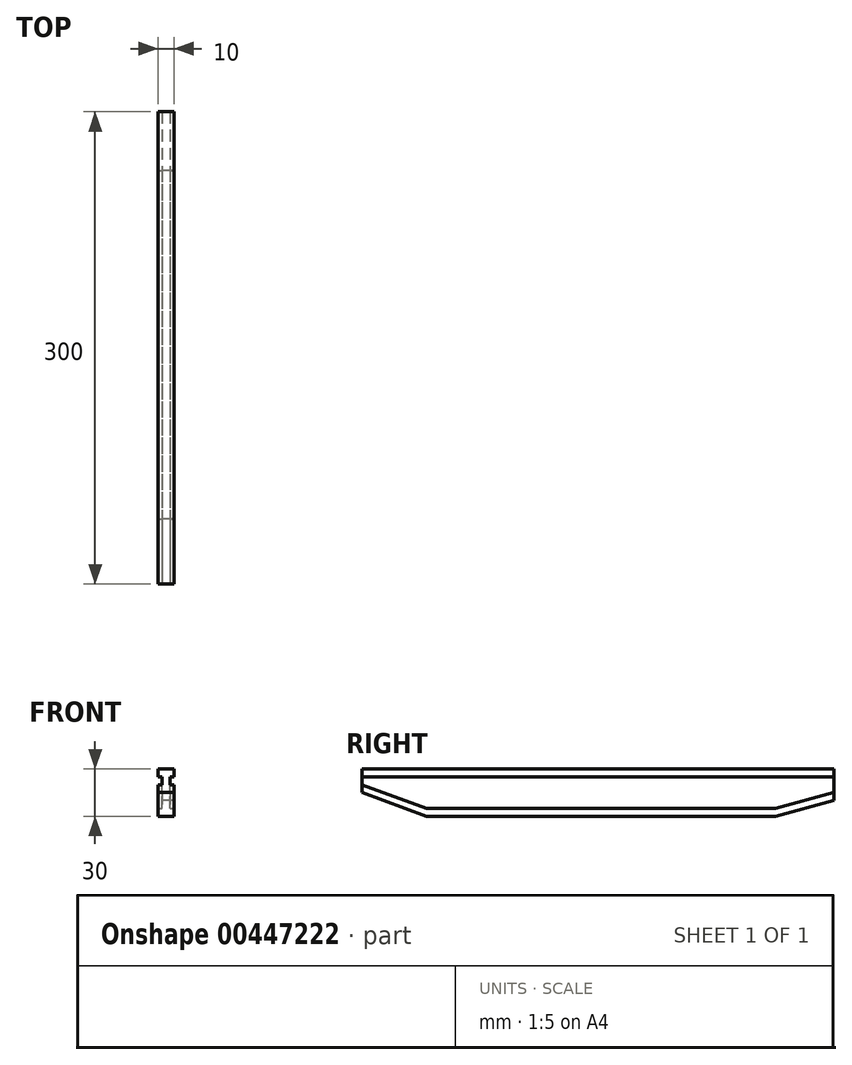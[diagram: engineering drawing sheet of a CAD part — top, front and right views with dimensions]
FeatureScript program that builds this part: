
annotation { "Feature Type Name" : "Feature", "Feature Type Description" : "" }
export const myFeature = defineFeature(function(context is Context, id is Id, definition is map)
    precondition{}
    {
        {
            var Q0;
            Q0=qCreatedBy(makeId("Right.planeOp"),FACE);
            var sketch = newSketch(context, id + "F0", { "sketchPlane" : qUnion([Q0])});
            skLineSegment(sketch, "E0", {"start": v(0, 0) * mm, "end": v(-300, 0) * mm});
            skLineSegment(sketch, "E1", {"start": v(-300, 0) * mm, "end": v(-300, -15) * mm});
            skLineSegment(sketch, "E2", {"start": v(-300, -15) * mm, "end": v(-258.79, -30) * mm});
            skLineSegment(sketch, "E3", {"start": v(-258.79, -30) * mm, "end": v(-37.32, -30) * mm});
            skLineSegment(sketch, "E4", {"start": v(-37.32, -30) * mm, "end": v(0, -20) * mm});
            skLineSegment(sketch, "E5", {"start": v(0, -20) * mm, "end": v(0, 0) * mm});
            skSolve(sketch);
        }
        {
            var Q0;
            Q0 = qSketchRegion(id + "F0", true);
            extrude(context, id + "F1", {"entities" : qUnion([Q0]), "endBound" : BoundingType.SYMMETRIC, "depth" : 5 * mm, "offsetDistance" : 25 * mm});
        }
        {
            var Q0;
            Q0=qCreatedBy(makeId("Front.planeOp"),FACE);
            var sketch = newSketch(context, id + "F2", { "sketchPlane" : qUnion([Q0])});
            skLineSegment(sketch, "E6.bottom", {"start": v(-5, 0) * mm, "end": v(5, 0) * mm});
            skLineSegment(sketch, "E6.top", {"start": v(-5, -5) * mm, "end": v(5, -5) * mm});
            skLineSegment(sketch, "E6.left", {"start": v(-5, 0) * mm, "end": v(-5, -5) * mm});
            skLineSegment(sketch, "E6.right", {"start": v(5, 0) * mm, "end": v(5, -5) * mm});
            skPoint(sketch, "E6.middle", {"position": v(0, -2.5) * mm});
            skSolve(sketch);
        }
        {
            var Q0;
            Q0 = qSketchRegion(id + "F2", true);
            var Q1;
            Q1=makeQuery(id+"F1.opExtrude","SWEPT_FACE",FACE,{"disambiguationData":[OSD([sQuery(id+"F0.wireOp",EDGE,"E1")])]});
            extrude(context, id + "F3", {"entities" : qUnion([Q0]), "operationType" : NewBodyOperationType.ADD, "endBound" : BoundingType.UP_TO_SURFACE, "depth" : 25 * mm, "endBoundEntityFace" : qUnion([Q1]), "offsetDistance" : 25 * mm});
        }
        {
            var Q0;
            Q0=qCreatedBy(makeId("Front.planeOp"),FACE);
            var sketch = newSketch(context, id + "F4", { "sketchPlane" : qUnion([Q0])});
            skLineSegment(sketch, "E7.bottom", {"start": v(-5, -20) * mm, "end": v(5, -20) * mm});
            skLineSegment(sketch, "E7.top", {"start": v(-5, -15) * mm, "end": v(5, -15) * mm});
            skLineSegment(sketch, "E7.left", {"start": v(-5, -20) * mm, "end": v(-5, -15) * mm});
            skLineSegment(sketch, "E7.right", {"start": v(5, -20) * mm, "end": v(5, -15) * mm});
            skPoint(sketch, "E7.middle", {"position": v(0, -17.5) * mm});
            skSolve(sketch);
        }
        {
            var Q0;
            Q0 = qSketchRegion(id + "F4", true);
            var Q1;
            Q1=makeQuery(id+"F1.opExtrude","CAP_EDGE",EDGE,{"disambiguationData":[OSD([sQuery(id+"F0.wireOp",EDGE,"E4")])],"isStart":false});
            var Q2;
            Q2=makeQuery(id+"F1.opExtrude","CAP_EDGE",EDGE,{"disambiguationData":[OSD([sQuery(id+"F0.wireOp",EDGE,"E3")])],"isStart":false});
            var Q3;
            Q3=makeQuery(id+"F1.opExtrude","CAP_EDGE",EDGE,{"disambiguationData":[OSD([sQuery(id+"F0.wireOp",EDGE,"E2")])],"isStart":false});
            sweep(context, id + "F5", {"operationType" : NewBodyOperationType.ADD, "profiles" : qUnion([Q0]), "path" : qUnion([Q1, Q2, Q3]), "keepProfileOrientation" : true});
        }
    });
